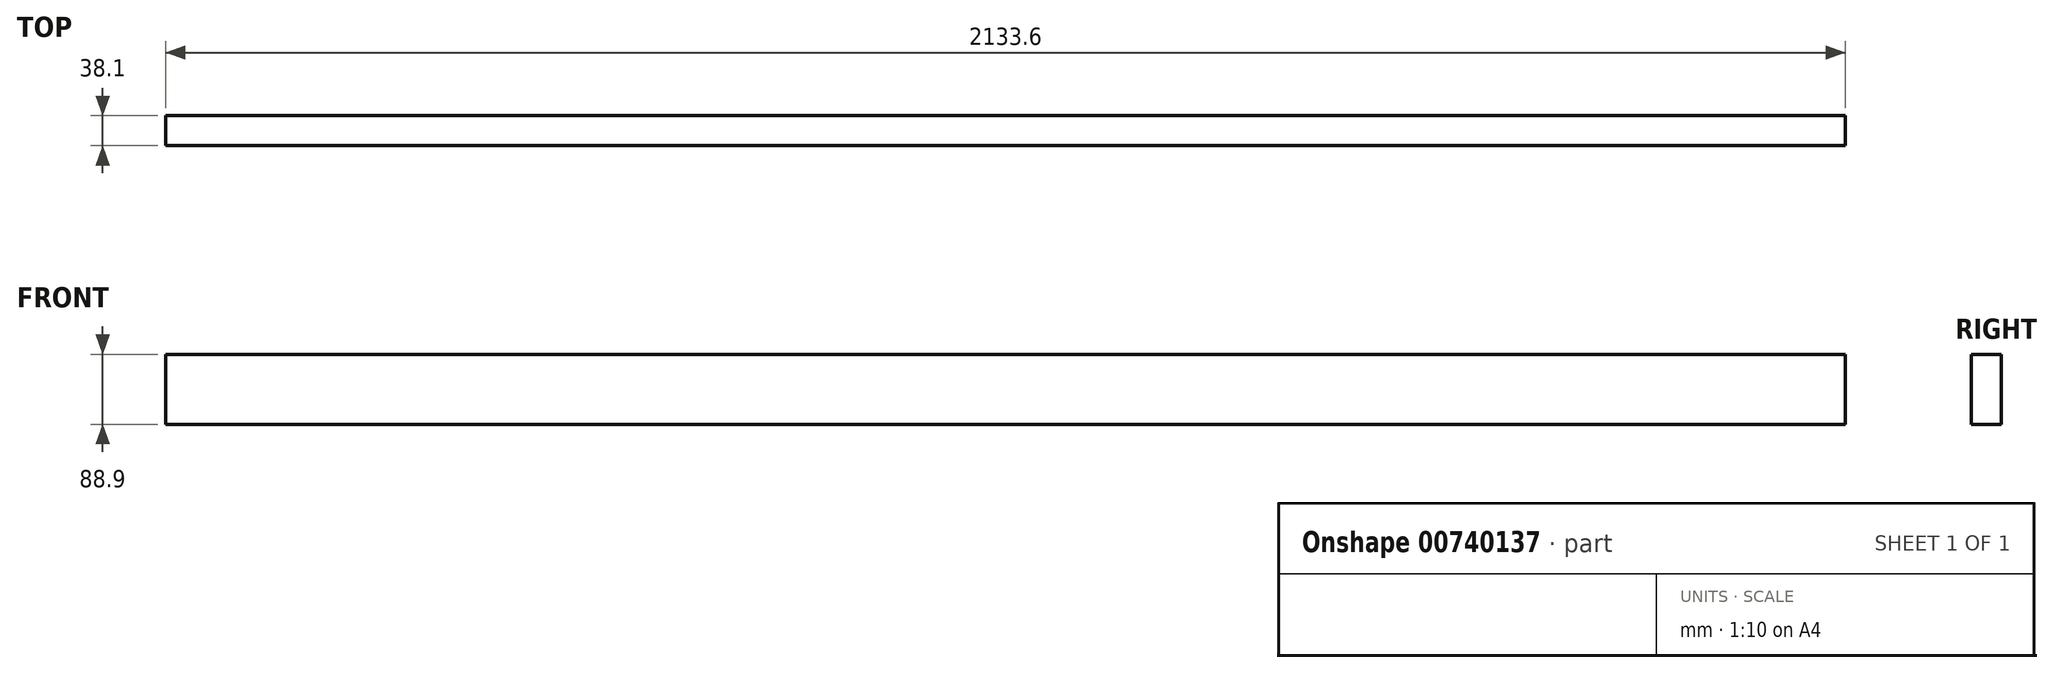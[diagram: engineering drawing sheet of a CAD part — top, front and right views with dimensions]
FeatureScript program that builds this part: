
annotation { "Feature Type Name" : "Feature", "Feature Type Description" : "" }
export const myFeature = defineFeature(function(context is Context, id is Id, definition is map)
    precondition{}
    {
        {
            var Q0;
            Q0=qCreatedBy(makeId("Right.planeOp"),FACE);
            var sketch = newSketch(context, id + "F0", { "sketchPlane" : qUnion([Q0])});
            skLineSegment(sketch, "E0.bottom", {"start": v(-79.68, 85.36) * mm, "end": v(-41.58, 85.36) * mm});
            skLineSegment(sketch, "E0.top", {"start": v(-79.68, -3.54) * mm, "end": v(-41.58, -3.54) * mm});
            skLineSegment(sketch, "E0.left", {"start": v(-79.68, 85.36) * mm, "end": v(-79.68, -3.54) * mm});
            skLineSegment(sketch, "E0.right", {"start": v(-41.58, 85.36) * mm, "end": v(-41.58, -3.54) * mm});
            skSolve(sketch);
        }
        {
            var Q0;
            Q0=makeQuery(id+"F0.imprint","IMPRINT",FACE,{"disambiguationData":[TD([[makeQuery(id+"F0.imprint","IMPRINT",EDGE,{"derivedFrom":sQuery(id+"F0.wireOp",EDGE,"E0.bottom")}),-1.0]])]});
            extrude(context, id + "F1", {"entities" : qUnion([Q0]), "depth" : 2133.6 * mm, "offsetDistance" : 25.4 * mm});
        }
    });
